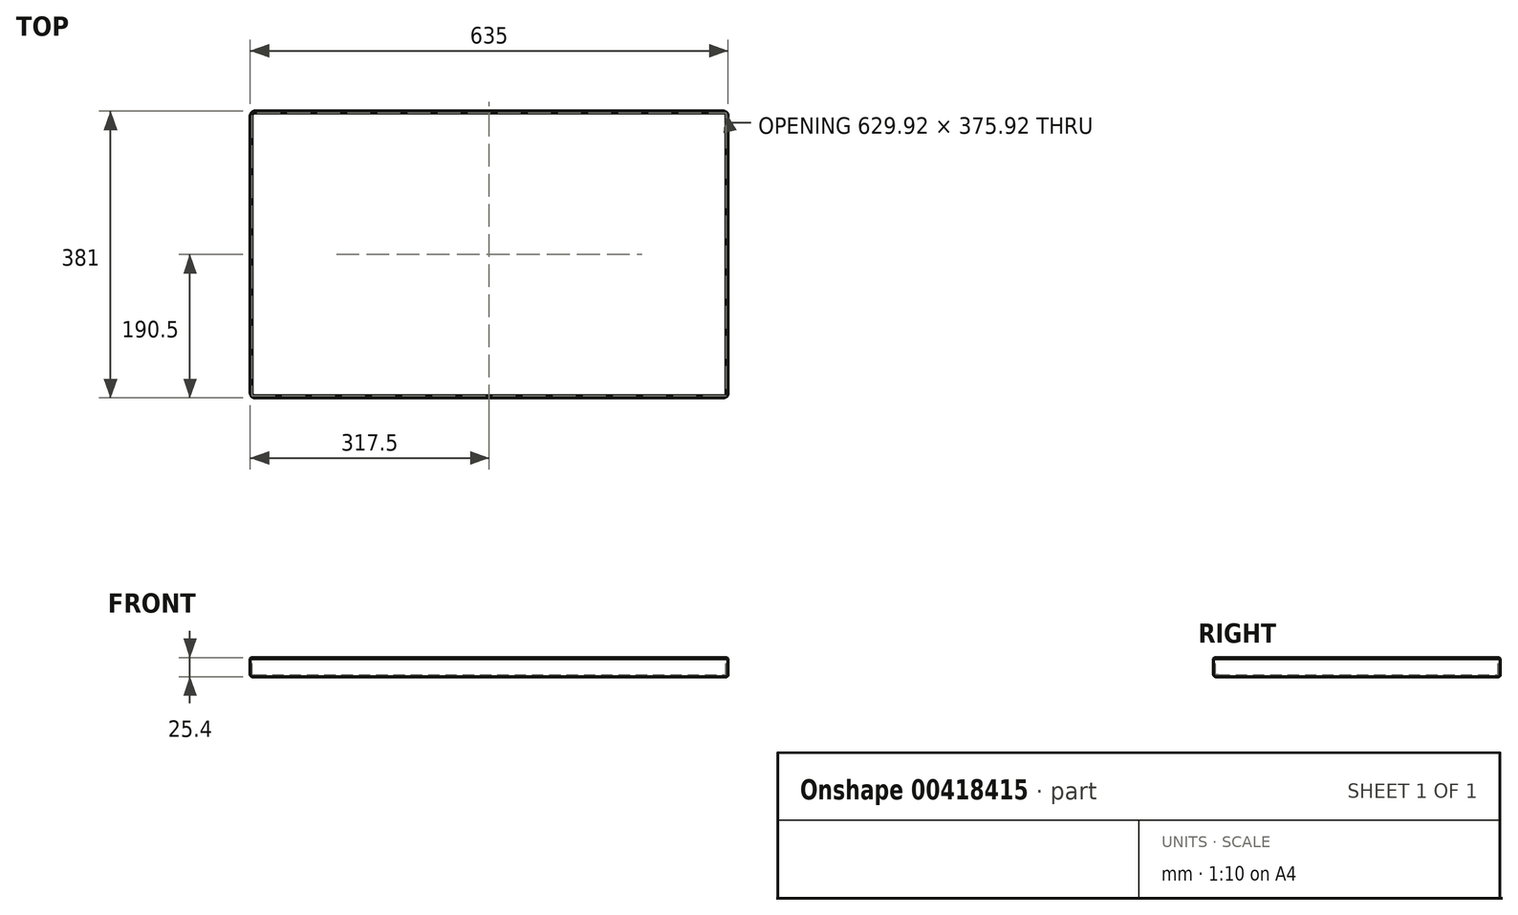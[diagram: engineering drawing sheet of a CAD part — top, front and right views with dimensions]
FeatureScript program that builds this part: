
annotation { "Feature Type Name" : "Feature", "Feature Type Description" : "" }
export const myFeature = defineFeature(function(context is Context, id is Id, definition is map)
    precondition{}
    {
        {
            var Q0;
            Q0=qCreatedBy(makeId("Top.planeOp"),FACE);
            var sketch = newSketch(context, id + "F0", { "sketchPlane" : qUnion([Q0])});
            skLineSegment(sketch, "E0.bottom", {"start": v(-311.15, -190.5) * mm, "end": v(311.15, -190.5) * mm});
            skLineSegment(sketch, "E0.top", {"start": v(-311.15, 190.5) * mm, "end": v(311.15, 190.5) * mm});
            skLineSegment(sketch, "E0.left", {"start": v(-317.5, -184.15) * mm, "end": v(-317.5, 184.15) * mm});
            skLineSegment(sketch, "E0.right", {"start": v(317.5, -184.15) * mm, "end": v(317.5, 184.15) * mm});
            skLineSegment(sketch, "E1", {"start": v(-317.5, 0) * mm, "end": v(317.5, 0) * mm, "construction": true});
            skLineSegment(sketch, "E2", {"start": v(0, 190.5) * mm, "end": v(0, -190.5) * mm, "construction": true});
            skPoint(sketch, "E3.visualSharp", {"position": v(-317.5, 190.5) * mm});
            skArc(sketch, "E3.filletArc", {"start": v(-311.15, 190.5) * mm, "mid": v(-315.64, 188.64) * mm, "end": v(-317.5, 184.15) * mm});
            skPoint(sketch, "E4.visualSharp", {"position": v(-317.5, -190.5) * mm});
            skArc(sketch, "E4.filletArc", {"start": v(-317.5, -184.15) * mm, "mid": v(-315.64, -188.64) * mm, "end": v(-311.15, -190.5) * mm});
            skPoint(sketch, "E5.visualSharp", {"position": v(317.5, -190.5) * mm});
            skArc(sketch, "E5.filletArc", {"start": v(311.15, -190.5) * mm, "mid": v(315.64, -188.64) * mm, "end": v(317.5, -184.15) * mm});
            skPoint(sketch, "E6.visualSharp", {"position": v(317.5, 190.5) * mm});
            skArc(sketch, "E6.filletArc", {"start": v(317.5, 184.15) * mm, "mid": v(315.64, 188.64) * mm, "end": v(311.15, 190.5) * mm});
            skSolve(sketch);
        }
        {
            var Q0;
            Q0 = qSketchRegion(id + "F0", true);
            extrude(context, id + "F1", {"entities" : qUnion([Q0]), "depth" : 25.4 * mm});
        }
        {
            var Q0;
            Q0=makeQuery(id+"F1.opExtrude","CAP_EDGE",EDGE,{"disambiguationData":[OSD([sQuery(id+"F0.wireOp",EDGE,"E0.bottom")])],"isStart":true});
            fillet(context, id + "F2", {"entities" : qUnion([Q0]), "radius" : 2.54 * mm, "tangentPropagation" : true, "allowEdgeOverflow" : false});
        }
        {
            var Q0;
            Q0=makeQuery(id+"F1.opExtrude","CAP_FACE",FACE,{"disambiguationData":[OSD([sQuery(id+"F0.wireOp",EDGE,"E0.bottom"),sQuery(id+"F0.wireOp",EDGE,"E0.top"),sQuery(id+"F0.wireOp",EDGE,"E0.left"),sQuery(id+"F0.wireOp",EDGE,"E0.right"),sQuery(id+"F0.wireOp",EDGE,"E3.filletArc"),sQuery(id+"F0.wireOp",EDGE,"E4.filletArc"),sQuery(id+"F0.wireOp",EDGE,"E5.filletArc"),sQuery(id+"F0.wireOp",EDGE,"E6.filletArc")])],"isStart":false});
            shell(context, id + "F3", {"entities" : qUnion([Q0]), "thickness" : 2.54 * mm});
        }
        {
            var Q0;
            Q0=makeQuery(id+"F1.opExtrude","CAP_EDGE",EDGE,{"disambiguationData":[OSD([sQuery(id+"F0.wireOp",EDGE,"E0.top")])],"isStart":false});
            chamfer(context, id + "F4", {"entities" : qUnion([Q0]), "width" : 1.27 * mm, "tangentPropagation" : true});
        }
    });
